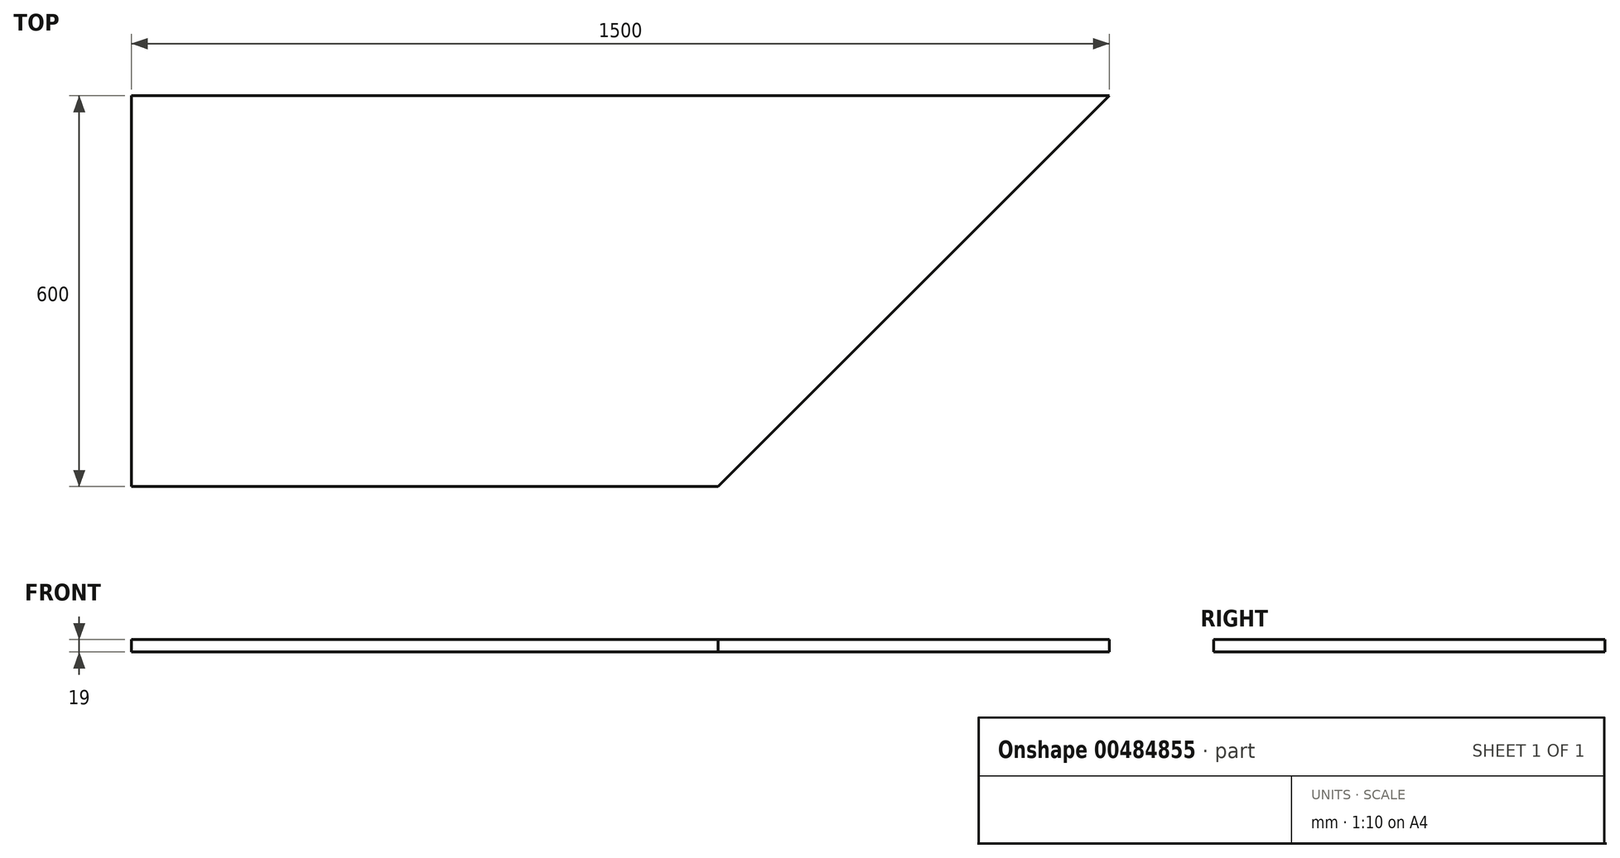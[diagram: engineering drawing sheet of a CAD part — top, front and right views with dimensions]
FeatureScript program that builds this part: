
annotation { "Feature Type Name" : "Feature", "Feature Type Description" : "" }
export const myFeature = defineFeature(function(context is Context, id is Id, definition is map)
    precondition{}
    {
        {
            var Q0;
            Q0=qCreatedBy(makeId("Top.planeOp"),FACE);
            var sketch = newSketch(context, id + "F0", { "sketchPlane" : qUnion([Q0])});
            skLineSegment(sketch, "E0", {"start": v(-98.02, 275.17) * mm, "end": v(-98.02, -324.83) * mm});
            skLineSegment(sketch, "E1", {"start": v(-98.02, 275.17) * mm, "end": v(1401.98, 275.17) * mm});
            skLineSegment(sketch, "E2", {"start": v(-98.02, -324.83) * mm, "end": v(801.98, -324.83) * mm});
            skLineSegment(sketch, "E3", {"start": v(801.98, -324.83) * mm, "end": v(1401.98, 275.17) * mm});
            skSolve(sketch);
        }
        {
            var Q0;
            Q0 = qSketchRegion(id + "F0", true);
            extrude(context, id + "F1", {"entities" : qUnion([Q0]), "depth" : 19 * mm});
        }
    });
